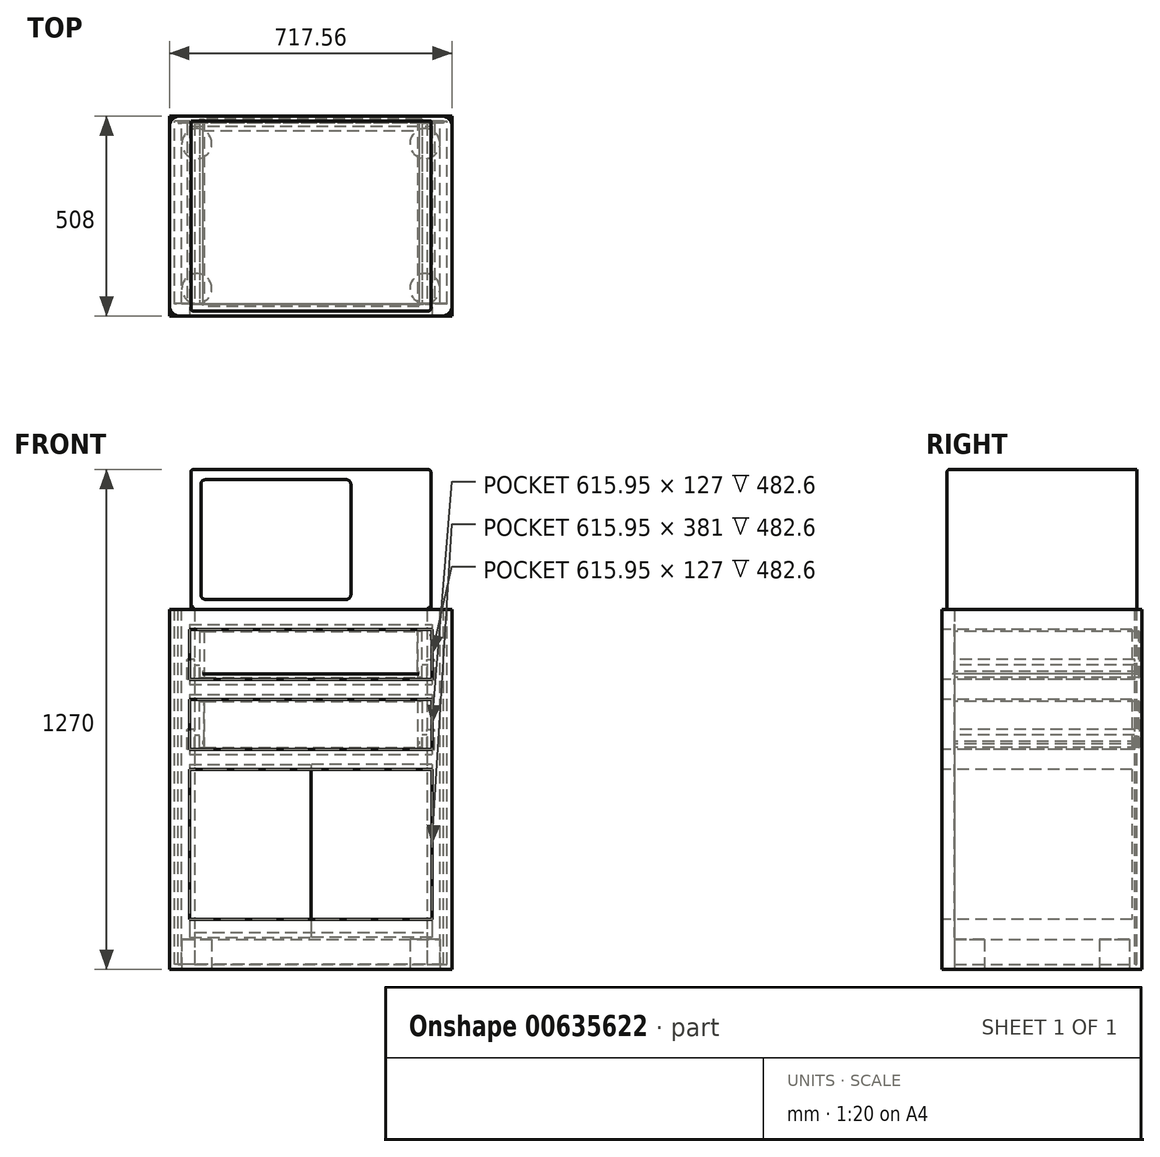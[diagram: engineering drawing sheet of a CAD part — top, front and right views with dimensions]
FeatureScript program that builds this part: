
annotation { "Feature Type Name" : "Feature", "Feature Type Description" : "" }
export const myFeature = defineFeature(function(context is Context, id is Id, definition is map)
    precondition{}
    {
        {
            assignVariable(context, id + "F0", {"name" : "ply_1_4", "anyValue" : 7 / 32});
        }
        {
            assignVariable(context, id + "F1", {"name" : "ply_1_2", "anyValue" : 15 / 32});
        }
        {
            assignVariable(context, id + "F2", {"name" : "ply_3_4", "anyValue" : 23 / 32});
        }
        {
            assignVariable(context, id + "F3", {"name" : "wood", "anyValue" : 3 / 4});
        }
        {
            var Q0;
            Q0=qCreatedBy(makeId("Top.planeOp"),FACE);
            cPlane(context, id + "F4", {"entities" : qUnion([Q0]), "cplaneType" : CPlaneType.OFFSET, "offset" : 914.4 * mm, "width" : 152.4 * mm, "height" : 152.4 * mm});
        }
        {
            var Q0;
            Q0=qCreatedBy(makeId("Top.planeOp"),FACE);
            cPlane(context, id + "F5", {"entities" : qUnion([Q0]), "cplaneType" : CPlaneType.OFFSET, "offset" : 12.7 * mm, "width" : 152.4 * mm, "height" : 152.4 * mm});
        }
        {
            var Q0;
            Q0=qCreatedBy(id+"F4.planeOp",FACE);
            var sketch = newSketch(context, id + "F6", { "sketchPlane" : qUnion([Q0])});
            skLineSegment(sketch, "E0.bottom", {"start": v(304.8, -241.3) * mm, "end": v(-304.8, -241.3) * mm});
            skLineSegment(sketch, "E0.top", {"start": v(304.8, 241.3) * mm, "end": v(-304.8, 241.3) * mm});
            skLineSegment(sketch, "E0.left", {"start": v(304.8, -241.3) * mm, "end": v(304.8, 241.3) * mm});
            skLineSegment(sketch, "E0.right", {"start": v(-304.8, -241.3) * mm, "end": v(-304.8, 241.3) * mm});
            skPoint(sketch, "E0.middle", {"position": v(0, 0) * mm});
            skSolve(sketch);
        }
        {
            var Q0;
            Q0=qSketchRegion(id+"F6",true);
            extrude(context, id + "F7", {"entities" : qUnion([Q0]), "depth" : 355.6 * mm, "offsetDistance" : 25.4 * mm});
        }
        {
            var Q0;
            Q0=makeQuery(id+"F7.opExtrude","SWEPT_FACE",FACE,{"disambiguationData":[OSD([sQuery(id+"F6.wireOp",EDGE,"E0.bottom")])]});
            var sketch = newSketch(context, id + "F8", { "sketchPlane" : qUnion([Q0])});
            skLineSegment(sketch, "E1.bottom", {"start": v(88.9, 939.8) * mm, "end": v(-266.7, 939.8) * mm});
            skLineSegment(sketch, "E1.top", {"start": v(88.9, 1244.6) * mm, "end": v(-266.7, 1244.6) * mm});
            skLineSegment(sketch, "E1.left", {"start": v(101.6, 952.5) * mm, "end": v(101.6, 1231.9) * mm});
            skLineSegment(sketch, "E1.right", {"start": v(-279.4, 952.5) * mm, "end": v(-279.4, 1231.9) * mm});
            skPoint(sketch, "E1.middle", {"position": v(-88.9, 1092.2) * mm});
            skPoint(sketch, "E2.visualSharp", {"position": v(-279.4, 1244.6) * mm});
            skArc(sketch, "E2.filletArc", {"start": v(-266.7, 1244.6) * mm, "mid": v(-275.68, 1240.88) * mm, "end": v(-279.4, 1231.9) * mm});
            skPoint(sketch, "E3.visualSharp", {"position": v(-279.4, 939.8) * mm});
            skArc(sketch, "E3.filletArc", {"start": v(-279.4, 952.5) * mm, "mid": v(-275.68, 943.52) * mm, "end": v(-266.7, 939.8) * mm});
            skPoint(sketch, "E4.visualSharp", {"position": v(101.6, 939.8) * mm});
            skArc(sketch, "E4.filletArc", {"start": v(88.9, 939.8) * mm, "mid": v(97.88, 943.52) * mm, "end": v(101.6, 952.5) * mm});
            skPoint(sketch, "E5.visualSharp", {"position": v(101.6, 1244.6) * mm});
            skArc(sketch, "E5.filletArc", {"start": v(101.6, 1231.9) * mm, "mid": v(97.88, 1240.88) * mm, "end": v(88.9, 1244.6) * mm});
            skSolve(sketch);
        }
        {
            var Q0;
            Q0 = qSketchRegion(id + "F8", true);
            extrude(context, id + "F9", {"entities" : qUnion([Q0]), "operationType" : NewBodyOperationType.REMOVE, "oppositeDirection" : true, "depth" : 1.59 * mm, "offsetDistance" : 25.4 * mm});
        }
        {
            var Q0;
            Q0=makeQuery(id+"F7.opExtrude","CAP_EDGE",EDGE,{"disambiguationData":[OSD([sQuery(id+"F6.wireOp",EDGE,"E0.right")])],"isStart":false});
            var Q1;
            Q1=makeQuery(id+"F7.opExtrude","CAP_EDGE",EDGE,{"disambiguationData":[OSD([sQuery(id+"F6.wireOp",EDGE,"E0.left")])],"isStart":false});
            var Q2;
            Q2=makeQuery(id+"F7.opExtrude","SWEPT_FACE",FACE,{"disambiguationData":[OSD([sQuery(id+"F6.wireOp",EDGE,"E0.bottom")])]});
            fillet(context, id + "F10", {"entities" : qUnion([Q0, Q1, Q2]), "radius" : 6.35 * mm, "tangentPropagation" : true, "allowEdgeOverflow" : false});
        }
        {
            var Q0;
            Q0=qCreatedBy(makeId("Top.planeOp"),FACE);
            var sketch = newSketch(context, id + "F11", { "sketchPlane" : qUnion([Q0])});
            skLineSegment(sketch, "E6.bottom", {"start": v(-358.78, -254) * mm, "end": v(358.78, -254) * mm});
            skLineSegment(sketch, "E6.top", {"start": v(-358.78, 254) * mm, "end": v(358.78, 254) * mm});
            skLineSegment(sketch, "E6.left", {"start": v(-358.78, -254) * mm, "end": v(-358.78, 254) * mm});
            skLineSegment(sketch, "E6.right", {"start": v(358.78, -254) * mm, "end": v(358.78, 254) * mm});
            skPoint(sketch, "E6.middle", {"position": v(0, 0) * mm});
            skSolve(sketch);
        }
        {
            var Q0;
            Q0=qSketchRegion(id+"F11",true);
            extrude(context, id + "F12", {"entities" : qUnion([Q0]), "depth" : 914.4 * mm, "offsetDistance" : 25.4 * mm});
        }
        {
            var Q0;
            Q0=makeQuery(id+"F12.opExtrude","SWEPT_FACE",FACE,{"disambiguationData":[OSD([sQuery(id+"F11.wireOp",EDGE,"E6.bottom")])]});
            var sketch = newSketch(context, id + "F13", { "sketchPlane" : qUnion([Q0])});
            skLineSegment(sketch, "E7.bottom", {"start": v(-307.98, 863.6) * mm, "end": v(307.98, 863.6) * mm});
            skLineSegment(sketch, "E7.top", {"start": v(-307.98, 736.6) * mm, "end": v(307.98, 736.6) * mm});
            skLineSegment(sketch, "E7.left", {"start": v(-307.98, 863.6) * mm, "end": v(-307.98, 736.6) * mm});
            skLineSegment(sketch, "E7.right", {"start": v(307.98, 863.6) * mm, "end": v(307.98, 736.6) * mm});
            skLineSegment(sketch, "E8.bottom", {"start": v(-307.98, 508) * mm, "end": v(307.98, 508) * mm});
            skLineSegment(sketch, "E8.top", {"start": v(-307.98, 127) * mm, "end": v(307.98, 127) * mm});
            skLineSegment(sketch, "E8.left", {"start": v(-307.98, 508) * mm, "end": v(-307.98, 127) * mm});
            skLineSegment(sketch, "E8.right", {"start": v(307.98, 508) * mm, "end": v(307.98, 127) * mm});
            skLineSegment(sketch, "E9.bottom", {"start": v(-307.98, 685.8) * mm, "end": v(307.98, 685.8) * mm});
            skLineSegment(sketch, "E9.top", {"start": v(-307.98, 558.8) * mm, "end": v(307.98, 558.8) * mm});
            skLineSegment(sketch, "E9.left", {"start": v(-307.98, 685.8) * mm, "end": v(-307.98, 558.8) * mm});
            skLineSegment(sketch, "E9.right", {"start": v(307.98, 685.8) * mm, "end": v(307.98, 558.8) * mm});
            skLineSegment(sketch, "E10.bottom", {"start": v(295.28, 850.9) * mm, "end": v(-295.28, 850.9) * mm, "construction": true});
            skLineSegment(sketch, "E10.top", {"start": v(295.28, 749.3) * mm, "end": v(-295.28, 749.3) * mm, "construction": true});
            skLineSegment(sketch, "E10.left", {"start": v(295.28, 850.9) * mm, "end": v(295.28, 749.3) * mm, "construction": true});
            skLineSegment(sketch, "E10.right", {"start": v(-295.28, 850.9) * mm, "end": v(-295.28, 749.3) * mm, "construction": true});
            skLineSegment(sketch, "E11.bottom", {"start": v(295.27, 673.1) * mm, "end": v(-295.28, 673.1) * mm, "construction": true});
            skLineSegment(sketch, "E11.top", {"start": v(295.27, 571.5) * mm, "end": v(-295.28, 571.5) * mm, "construction": true});
            skLineSegment(sketch, "E11.left", {"start": v(295.27, 673.1) * mm, "end": v(295.27, 571.5) * mm, "construction": true});
            skLineSegment(sketch, "E11.right", {"start": v(-295.28, 673.1) * mm, "end": v(-295.28, 571.5) * mm, "construction": true});
            skSolve(sketch);
        }
        {
            var Q0;
            Q0=qSketchRegion(id+"F13",true);
            extrude(context, id + "F14", {"entities" : qUnion([Q0]), "operationType" : NewBodyOperationType.REMOVE, "oppositeDirection" : true, "depth" : 482.6 * mm, "offsetDistance" : 25.4 * mm});
        }
        {
            var Q0;
            Q0=qCreatedBy(id+"F4.planeOp",FACE);
            var sketch = newSketch(context, id + "F15", { "sketchPlane" : qUnion([Q0])});
            skLineSegment(sketch, "E12.bottom", {"start": v(333.38, -254) * mm, "end": v(-333.38, -254) * mm});
            skLineSegment(sketch, "E12.top", {"start": v(333.38, 254) * mm, "end": v(-333.38, 254) * mm});
            skLineSegment(sketch, "E12.left", {"start": v(358.78, -228.6) * mm, "end": v(358.78, 228.6) * mm});
            skLineSegment(sketch, "E12.right", {"start": v(-358.78, -228.6) * mm, "end": v(-358.78, 228.6) * mm});
            skPoint(sketch, "E12.middle", {"position": v(0, 0) * mm});
            skPoint(sketch, "E13.visualSharp", {"position": v(-358.78, 254) * mm});
            skArc(sketch, "E13.filletArc", {"start": v(-333.38, 254) * mm, "mid": v(-351.34, 246.56) * mm, "end": v(-358.77, 228.6) * mm});
            skPoint(sketch, "E14.visualSharp", {"position": v(-358.77, -254) * mm});
            skArc(sketch, "E14.filletArc", {"start": v(-358.77, -228.6) * mm, "mid": v(-351.34, -246.56) * mm, "end": v(-333.38, -254) * mm});
            skPoint(sketch, "E15.visualSharp", {"position": v(358.78, -254) * mm});
            skArc(sketch, "E15.filletArc", {"start": v(333.38, -254) * mm, "mid": v(351.34, -246.56) * mm, "end": v(358.78, -228.6) * mm});
            skPoint(sketch, "E16.visualSharp", {"position": v(358.78, 254) * mm});
            skArc(sketch, "E16.filletArc", {"start": v(358.78, 228.6) * mm, "mid": v(351.34, 246.56) * mm, "end": v(333.38, 254) * mm});
            skSolve(sketch);
        }
        {
            var Q0;
            Q0 = qSketchRegion(id + "F15", true);
            extrude(context, id + "F16", {"entities" : qUnion([Q0]), "depth" : (getVariable(context, 'ply_3_4')) * mm, "offsetDistance" : 25.4 * mm});
        }
        {
            var Q0;
            Q0=qCreatedBy(id+"F4.planeOp",FACE);
            var sketch = newSketch(context, id + "F17", { "sketchPlane" : qUnion([Q0])});
            skLineSegment(sketch, "E17.left", {"start": v(-327.82, 235.74) * mm, "end": v(-327.82, -222.25) * mm});
            skLineSegment(sketch, "E17.right", {"start": v(-346.08, 241.3) * mm, "end": v(-346.08, -222.25) * mm});
            skPoint(sketch, "E17.middle", {"position": v(-336.95, 9.52) * mm});
            skLineSegment(sketch, "E18", {"start": v(-346.08, -222.25) * mm, "end": v(-327.82, -222.25) * mm});
            skLineSegment(sketch, "E19", {"start": v(-346.08, 241.3) * mm, "end": v(-337.34, 241.3) * mm});
            skLineSegment(sketch, "E20", {"start": v(-327.82, 235.74) * mm, "end": v(-337.34, 235.74) * mm});
            skLineSegment(sketch, "E21", {"start": v(-337.34, 235.74) * mm, "end": v(-337.34, 241.3) * mm});
            skLineSegment(sketch, "E22.bottom", {"start": v(-337.34, 235.74) * mm, "end": v(337.34, 235.74) * mm});
            skLineSegment(sketch, "E22.top", {"start": v(-337.34, 241.3) * mm, "end": v(337.34, 241.3) * mm});
            skLineSegment(sketch, "E22.right", {"start": v(337.34, 235.74) * mm, "end": v(337.34, 241.3) * mm});
            skLineSegment(sketch, "E23.MirrorCS", {"start": v(346.08, 241.3) * mm, "end": v(337.34, 241.3) * mm});
            skLineSegment(sketch, "E24.MirrorCS", {"start": v(327.82, 235.74) * mm, "end": v(337.34, 235.74) * mm});
            skLineSegment(sketch, "E25.MirrorCS", {"start": v(327.82, 235.74) * mm, "end": v(327.82, -222.25) * mm});
            skLineSegment(sketch, "E26.MirrorCS", {"start": v(346.08, 241.3) * mm, "end": v(346.08, -222.25) * mm});
            skPoint(sketch, "E27.MirrorP", {"position": v(336.95, 9.52) * mm});
            skLineSegment(sketch, "E28.MirrorCS", {"start": v(346.08, -222.25) * mm, "end": v(327.82, -222.25) * mm});
            skSolve(sketch);
        }
        {
            var Q0;
            Q0 = qSketchRegion(id + "F17", true);
            var Q1;
            Q1=qCreatedBy(id+"F5.planeOp",FACE);
            extrude(context, id + "F18", {"entities" : qUnion([Q0]), "endBound" : BoundingType.UP_TO_SURFACE, "oppositeDirection" : true, "depth" : 25.4 * mm, "endBoundEntityFace" : qUnion([Q1]), "offsetDistance" : 25.4 * mm});
        }
        {
            var Q0;
            Q0=qCreatedBy(makeId("Top.planeOp"),FACE);
            var sketch = newSketch(context, id + "F19", { "sketchPlane" : qUnion([Q0])});
            skCircle(sketch, "E29", {"center": v(-289.72, -184.15) * mm, "radius": 38.1 * mm});
            skCircle(sketch, "E30.MirrorC", {"center": v(289.72, -184.15) * mm, "radius": 38.1 * mm});
            skCircle(sketch, "E31.MirrorC", {"center": v(-289.72, 184.15) * mm, "radius": 38.1 * mm});
            skCircle(sketch, "E32.MirrorC", {"center": v(289.72, 184.15) * mm, "radius": 38.1 * mm});
            skSolve(sketch);
        }
        {
            var Q0;
            Q0 = qSketchRegion(id + "F19", true);
            extrude(context, id + "F20", {"entities" : qUnion([Q0]), "depth" : 76.2 * mm, "offsetDistance" : 25.4 * mm});
        }
        {
            var Q0;
            Q0=makeQuery(id+"F18.opExtrude","SWEPT_FACE",FACE,{"disambiguationData":[OSD([sQuery(id+"F17.wireOp",EDGE,"E18")])]});
            var sketch = newSketch(context, id + "F21", { "sketchPlane" : qUnion([Q0])});
            skLineSegment(sketch, "E33.0", {"start": v(-346.08, 12.7) * mm, "end": v(-346.08, 914.4) * mm});
            skLineSegment(sketch, "E34", {"start": v(-346.08, 914.4) * mm, "end": v(-295.28, 914.4) * mm});
            skLineSegment(sketch, "E35", {"start": v(-295.28, 914.4) * mm, "end": v(-295.28, 12.7) * mm});
            skLineSegment(sketch, "E36", {"start": v(-295.28, 12.7) * mm, "end": v(-346.08, 12.7) * mm});
            skLineSegment(sketch, "E37.MirrorCS", {"start": v(295.28, 12.7) * mm, "end": v(346.08, 12.7) * mm});
            skLineSegment(sketch, "E38.MirrorCS", {"start": v(346.08, 914.4) * mm, "end": v(295.28, 914.4) * mm});
            skLineSegment(sketch, "E39.MirrorCS", {"start": v(295.28, 914.4) * mm, "end": v(295.28, 12.7) * mm});
            skLineSegment(sketch, "E40.MirrorCS", {"start": v(346.08, 12.7) * mm, "end": v(346.08, 914.4) * mm});
            skLineSegment(sketch, "E41.bottom", {"start": v(-295.27, 914.4) * mm, "end": v(295.27, 914.4) * mm});
            skLineSegment(sketch, "E41.top", {"start": v(-295.27, 863.6) * mm, "end": v(295.27, 863.6) * mm});
            skLineSegment(sketch, "E41.left", {"start": v(-295.27, 914.4) * mm, "end": v(-295.27, 863.6) * mm});
            skLineSegment(sketch, "E41.right", {"start": v(295.27, 914.4) * mm, "end": v(295.27, 863.6) * mm});
            skLineSegment(sketch, "E42.bottom", {"start": v(-295.27, 736.6) * mm, "end": v(295.27, 736.6) * mm});
            skLineSegment(sketch, "E42.top", {"start": v(-295.27, 685.8) * mm, "end": v(295.27, 685.8) * mm});
            skLineSegment(sketch, "E42.left", {"start": v(-295.27, 736.6) * mm, "end": v(-295.27, 685.8) * mm});
            skLineSegment(sketch, "E42.right", {"start": v(295.27, 736.6) * mm, "end": v(295.27, 685.8) * mm});
            skLineSegment(sketch, "E43.bottom", {"start": v(-295.27, 558.8) * mm, "end": v(295.27, 558.8) * mm});
            skLineSegment(sketch, "E43.top", {"start": v(-295.27, 508) * mm, "end": v(295.27, 508) * mm});
            skLineSegment(sketch, "E43.left", {"start": v(-295.27, 558.8) * mm, "end": v(-295.27, 508) * mm});
            skLineSegment(sketch, "E43.right", {"start": v(295.27, 558.8) * mm, "end": v(295.27, 508) * mm});
            skLineSegment(sketch, "E44.bottom", {"start": v(-295.27, 94.46) * mm, "end": v(295.27, 94.46) * mm});
            skLineSegment(sketch, "E44.top", {"start": v(-295.27, 12.7) * mm, "end": v(295.27, 12.7) * mm});
            skLineSegment(sketch, "E44.left", {"start": v(-295.27, 94.46) * mm, "end": v(-295.27, 12.7) * mm});
            skLineSegment(sketch, "E44.right", {"start": v(295.27, 94.46) * mm, "end": v(295.27, 12.7) * mm});
            skSolve(sketch);
        }
        {
            var Q0;
            Q0 = qSketchRegion(id + "F21", true);
            extrude(context, id + "F22", {"entities" : qUnion([Q0]), "depth" : (getVariable(context, 'wood')) * mm, "offsetDistance" : 25.4 * mm});
        }
        {
            var Q0;
            Q0=makeQuery(id+"F20.opExtrude","CAP_FACE",FACE,{"disambiguationData":[OSD([sQuery(id+"F19.wireOp",EDGE,"E31.MirrorC")])],"isStart":false});
            var sketch = newSketch(context, id + "F23", { "sketchPlane" : qUnion([Q0])});
            skLineSegment(sketch, "E45.0", {"start": v(-327.82, -222.25) * mm, "end": v(-327.82, 235.74) * mm});
            skLineSegment(sketch, "E46.0", {"start": v(327.82, -222.25) * mm, "end": v(327.82, 235.74) * mm});
            skLineSegment(sketch, "E47", {"start": v(-327.82, -222.25) * mm, "end": v(327.82, -222.25) * mm});
            skLineSegment(sketch, "E48", {"start": v(327.82, 235.74) * mm, "end": v(-327.82, 235.74) * mm});
            skSolve(sketch);
        }
        {
            var Q0;
            Q0 = qSketchRegion(id + "F23", true);
            extrude(context, id + "F24", {"entities" : qUnion([Q0]), "depth" : (getVariable(context, 'ply_3_4')) * mm, "offsetDistance" : 25.4 * mm});
        }
        {
            var Q0;
            Q0=makeQuery(id+"F22.opExtrude","CAP_FACE",FACE,{"disambiguationData":[OSD([sQuery(id+"F21.wireOp",EDGE,"E33.0"),sQuery(id+"F21.wireOp",EDGE,"E34"),sQuery(id+"F21.wireOp",EDGE,"E35"),sQuery(id+"F21.wireOp",EDGE,"E36")])],"isStart":false});
            var sketch = newSketch(context, id + "F25", { "sketchPlane" : qUnion([Q0])});
            skLineSegment(sketch, "E49.bottom", {"start": v(-307.98, 876.3) * mm, "end": v(307.98, 876.3) * mm});
            skLineSegment(sketch, "E49.top", {"start": v(-307.98, 723.9) * mm, "end": v(307.98, 723.9) * mm});
            skLineSegment(sketch, "E49.left", {"start": v(-307.98, 876.3) * mm, "end": v(-307.98, 723.9) * mm});
            skLineSegment(sketch, "E49.right", {"start": v(307.98, 876.3) * mm, "end": v(307.98, 723.9) * mm});
            skLineSegment(sketch, "E50.bottom", {"start": v(-307.98, 698.5) * mm, "end": v(307.98, 698.5) * mm});
            skLineSegment(sketch, "E50.top", {"start": v(-307.98, 546.1) * mm, "end": v(307.98, 546.1) * mm});
            skLineSegment(sketch, "E50.left", {"start": v(-307.98, 698.5) * mm, "end": v(-307.98, 546.1) * mm});
            skLineSegment(sketch, "E50.right", {"start": v(307.98, 698.5) * mm, "end": v(307.98, 546.1) * mm});
            skLineSegment(sketch, "E51.bottom", {"start": v(-307.98, 520.7) * mm, "end": v(0, 520.7) * mm});
            skLineSegment(sketch, "E51.top", {"start": v(-307.98, 81.76) * mm, "end": v(0, 81.76) * mm});
            skLineSegment(sketch, "E51.left", {"start": v(-307.98, 520.7) * mm, "end": v(-307.98, 81.76) * mm});
            skLineSegment(sketch, "E51.right", {"start": v(0, 520.7) * mm, "end": v(0, 81.76) * mm});
            skLineSegment(sketch, "E52.MirrorCS", {"start": v(307.98, 81.76) * mm, "end": v(0, 81.76) * mm});
            skLineSegment(sketch, "E53.MirrorCS", {"start": v(307.98, 520.7) * mm, "end": v(0, 520.7) * mm});
            skLineSegment(sketch, "E54.MirrorCS", {"start": v(307.98, 520.7) * mm, "end": v(307.98, 81.76) * mm});
            skSolve(sketch);
        }
        {
            var Q0;
            Q0 = qSketchRegion(id + "F25", true);
            extrude(context, id + "F26", {"entities" : qUnion([Q0]), "depth" : (getVariable(context, 'wood')) * mm, "offsetDistance" : 25.4 * mm});
        }
        {
            var Q0;
            Q0=makeQuery(id+"F22.opExtrude","CAP_FACE",FACE,{"disambiguationData":[OSD([sQuery(id+"F21.wireOp",EDGE,"E33.0"),sQuery(id+"F21.wireOp",EDGE,"E34"),sQuery(id+"F21.wireOp",EDGE,"E35"),sQuery(id+"F21.wireOp",EDGE,"E36")])],"isStart":true});
            var sketch = newSketch(context, id + "F27", { "sketchPlane" : qUnion([Q0])});
            skLineSegment(sketch, "E55.bottom", {"start": v(-314.33, 787.4) * mm, "end": v(-295.28, 787.4) * mm});
            skLineSegment(sketch, "E55.top", {"start": v(-314.33, 736.6) * mm, "end": v(-295.28, 736.6) * mm});
            skLineSegment(sketch, "E55.left", {"start": v(-314.33, 787.4) * mm, "end": v(-314.33, 736.6) * mm});
            skLineSegment(sketch, "E55.right", {"start": v(-295.28, 787.4) * mm, "end": v(-295.28, 736.6) * mm});
            skLineSegment(sketch, "E56.bottom", {"start": v(-314.33, 609.6) * mm, "end": v(-295.28, 609.6) * mm});
            skLineSegment(sketch, "E56.top", {"start": v(-314.33, 558.8) * mm, "end": v(-295.28, 558.8) * mm});
            skLineSegment(sketch, "E56.left", {"start": v(-314.33, 609.6) * mm, "end": v(-314.33, 558.8) * mm});
            skLineSegment(sketch, "E56.right", {"start": v(-295.28, 609.6) * mm, "end": v(-295.28, 558.8) * mm});
            skLineSegment(sketch, "E57.MirrorCS", {"start": v(314.33, 558.8) * mm, "end": v(295.28, 558.8) * mm});
            skLineSegment(sketch, "E58.MirrorCS", {"start": v(314.33, 609.6) * mm, "end": v(295.28, 609.6) * mm});
            skLineSegment(sketch, "E59.MirrorCS", {"start": v(314.33, 736.6) * mm, "end": v(295.28, 736.6) * mm});
            skLineSegment(sketch, "E60.MirrorCS", {"start": v(314.33, 787.4) * mm, "end": v(295.28, 787.4) * mm});
            skLineSegment(sketch, "E61.MirrorCS", {"start": v(295.28, 609.6) * mm, "end": v(295.28, 558.8) * mm});
            skLineSegment(sketch, "E62.MirrorCS", {"start": v(295.28, 787.4) * mm, "end": v(295.28, 736.6) * mm});
            skLineSegment(sketch, "E63.MirrorCS", {"start": v(314.33, 609.6) * mm, "end": v(314.33, 558.8) * mm});
            skLineSegment(sketch, "E64.MirrorCS", {"start": v(314.33, 787.4) * mm, "end": v(314.33, 736.6) * mm});
            skSolve(sketch);
        }
        {
            var Q0;
            Q0 = qSketchRegion(id + "F27", true);
            var Q1;
            Q1=makeQuery(id+"F18.opExtrude","SWEPT_FACE",FACE,{"disambiguationData":[OSD([sQuery(id+"F17.wireOp",EDGE,"E22.bottom")])]});
            extrude(context, id + "F28", {"entities" : qUnion([Q0]), "endBound" : BoundingType.UP_TO_SURFACE, "depth" : 25.4 * mm, "endBoundEntityFace" : qUnion([Q1]), "offsetDistance" : 25.4 * mm});
        }
        {
            var Q0;
            Q0=makeQuery(id+"F28.opExtrude","CAP_FACE",FACE,{"disambiguationData":[OSD([sQuery(id+"F27.wireOp",EDGE,"E59.MirrorCS"),sQuery(id+"F27.wireOp",EDGE,"E60.MirrorCS"),sQuery(id+"F27.wireOp",EDGE,"E62.MirrorCS"),sQuery(id+"F27.wireOp",EDGE,"E64.MirrorCS")])],"isStart":true});
            var sketch = newSketch(context, id + "F29", { "sketchPlane" : qUnion([Q0])});
            skLineSegment(sketch, "E65.bottom", {"start": v(-295.28, 736.6) * mm, "end": v(-282.58, 736.6) * mm});
            skLineSegment(sketch, "E65.top", {"start": v(-295.28, 773.68) * mm, "end": v(-282.58, 773.68) * mm});
            skLineSegment(sketch, "E65.left", {"start": v(-295.28, 736.6) * mm, "end": v(-295.28, 773.68) * mm});
            skLineSegment(sketch, "E65.right", {"start": v(-282.58, 736.6) * mm, "end": v(-282.58, 773.68) * mm});
            skLineSegment(sketch, "E66.bottom", {"start": v(-295.28, 558.8) * mm, "end": v(-282.58, 558.8) * mm});
            skLineSegment(sketch, "E66.top", {"start": v(-295.28, 595.88) * mm, "end": v(-282.58, 595.88) * mm});
            skLineSegment(sketch, "E66.left", {"start": v(-295.28, 558.8) * mm, "end": v(-295.28, 595.88) * mm});
            skLineSegment(sketch, "E66.right", {"start": v(-282.58, 558.8) * mm, "end": v(-282.58, 595.88) * mm});
            skLineSegment(sketch, "E67.MirrorCS", {"start": v(295.28, 773.68) * mm, "end": v(282.58, 773.68) * mm});
            skLineSegment(sketch, "E68.MirrorCS", {"start": v(295.28, 736.6) * mm, "end": v(282.58, 736.6) * mm});
            skLineSegment(sketch, "E69.MirrorCS", {"start": v(295.28, 558.8) * mm, "end": v(282.58, 558.8) * mm});
            skLineSegment(sketch, "E70.MirrorCS", {"start": v(295.28, 595.88) * mm, "end": v(282.58, 595.88) * mm});
            skLineSegment(sketch, "E71.MirrorCS", {"start": v(282.58, 736.6) * mm, "end": v(282.58, 773.68) * mm});
            skLineSegment(sketch, "E72.MirrorCS", {"start": v(295.28, 736.6) * mm, "end": v(295.28, 773.68) * mm});
            skLineSegment(sketch, "E73.MirrorCS", {"start": v(282.58, 558.8) * mm, "end": v(282.58, 595.88) * mm});
            skLineSegment(sketch, "E74.MirrorCS", {"start": v(295.28, 558.8) * mm, "end": v(295.28, 595.88) * mm});
            skSolve(sketch);
        }
        {
            var Q0;
            Q0 = qSketchRegion(id + "F29", true);
            extrude(context, id + "F30", {"entities" : qUnion([Q0]), "oppositeDirection" : true, "depth" : 457.2 * mm, "offsetDistance" : 25.4 * mm});
        }
        {
            var Q0;
            Q0=makeQuery(id+"F22.opExtrude","CAP_FACE",FACE,{"disambiguationData":[OSD([sQuery(id+"F21.wireOp",EDGE,"E33.0"),sQuery(id+"F21.wireOp",EDGE,"E34"),sQuery(id+"F21.wireOp",EDGE,"E35"),sQuery(id+"F21.wireOp",EDGE,"E36")])],"isStart":false});
            var sketch = newSketch(context, id + "F31", { "sketchPlane" : qUnion([Q0])});
            skLineSegment(sketch, "E75.bottom", {"start": v(-282.58, 858.84) * mm, "end": v(-270.67, 858.84) * mm});
            skLineSegment(sketch, "E75.top", {"start": v(-282.58, 741.36) * mm, "end": v(-270.67, 741.36) * mm});
            skLineSegment(sketch, "E75.left", {"start": v(-282.58, 858.84) * mm, "end": v(-282.58, 741.36) * mm});
            skLineSegment(sketch, "E75.right", {"start": v(-270.67, 858.84) * mm, "end": v(-270.67, 756.44) * mm});
            skLineSegment(sketch, "E76", {"start": v(-270.67, 756.44) * mm, "end": v(-275.43, 756.44) * mm});
            skLineSegment(sketch, "E77", {"start": v(-275.43, 756.44) * mm, "end": v(-275.43, 750.89) * mm});
            skLineSegment(sketch, "E78", {"start": v(-275.43, 750.89) * mm, "end": v(-270.67, 750.89) * mm});
            skLineSegment(sketch, "E79.bottom", {"start": v(-282.58, 681.04) * mm, "end": v(-270.67, 681.04) * mm});
            skLineSegment(sketch, "E79.top", {"start": v(-282.58, 563.56) * mm, "end": v(-270.67, 563.56) * mm});
            skLineSegment(sketch, "E79.left", {"start": v(-282.58, 563.56) * mm, "end": v(-282.58, 681.04) * mm});
            skLineSegment(sketch, "E79.right", {"start": v(-270.67, 578.64) * mm, "end": v(-270.67, 681.04) * mm});
            skLineSegment(sketch, "E80", {"start": v(-270.67, 578.64) * mm, "end": v(-275.43, 578.64) * mm});
            skLineSegment(sketch, "E81", {"start": v(-275.43, 578.64) * mm, "end": v(-275.43, 573.09) * mm});
            skLineSegment(sketch, "E82", {"start": v(-270.67, 573.09) * mm, "end": v(-275.43, 573.09) * mm});
            skLineSegment(sketch, "E83.trimOffspring", {"start": v(-270.67, 563.56) * mm, "end": v(-270.67, 573.09) * mm});
            skLineSegment(sketch, "E84.MirrorCS", {"start": v(270.67, 756.44) * mm, "end": v(275.43, 756.44) * mm});
            skLineSegment(sketch, "E85.MirrorCS", {"start": v(270.67, 573.09) * mm, "end": v(275.43, 573.09) * mm});
            skLineSegment(sketch, "E86.MirrorCS", {"start": v(275.43, 578.64) * mm, "end": v(275.43, 573.09) * mm});
            skLineSegment(sketch, "E87.MirrorCS", {"start": v(270.67, 573.09) * mm, "end": v(270.67, 563.56) * mm});
            skLineSegment(sketch, "E88.MirrorCS", {"start": v(270.67, 578.64) * mm, "end": v(275.43, 578.64) * mm});
            skLineSegment(sketch, "E89.MirrorCS", {"start": v(275.43, 750.89) * mm, "end": v(270.67, 750.89) * mm});
            skLineSegment(sketch, "E90.MirrorCS", {"start": v(270.67, 750.89) * mm, "end": v(270.67, 741.36) * mm});
            skLineSegment(sketch, "E91.MirrorCS", {"start": v(275.43, 750.89) * mm, "end": v(275.43, 756.44) * mm});
            skLineSegment(sketch, "E92.MirrorCS", {"start": v(282.58, 681.04) * mm, "end": v(270.67, 681.04) * mm});
            skLineSegment(sketch, "E93.MirrorCS", {"start": v(282.58, 563.56) * mm, "end": v(270.67, 563.56) * mm});
            skLineSegment(sketch, "E94.MirrorCS", {"start": v(282.58, 858.84) * mm, "end": v(270.67, 858.84) * mm});
            skLineSegment(sketch, "E95.MirrorCS", {"start": v(282.58, 741.36) * mm, "end": v(270.67, 741.36) * mm});
            skLineSegment(sketch, "E96.MirrorCS", {"start": v(282.58, 681.04) * mm, "end": v(282.58, 563.56) * mm});
            skLineSegment(sketch, "E97.MirrorCS", {"start": v(270.67, 681.04) * mm, "end": v(270.67, 578.64) * mm});
            skLineSegment(sketch, "E98.MirrorCS", {"start": v(270.67, 756.44) * mm, "end": v(270.67, 858.84) * mm});
            skLineSegment(sketch, "E99.MirrorCS", {"start": v(282.58, 741.36) * mm, "end": v(282.58, 858.84) * mm});
            skLineSegment(sketch, "E100", {"start": v(-270.67, 750.89) * mm, "end": v(-270.67, 741.36) * mm});
            skSolve(sketch);
        }
        {
            var Q0;
            Q0 = qSketchRegion(id + "F31", true);
            extrude(context, id + "F32", {"entities" : qUnion([Q0]), "oppositeDirection" : true, "depth" : 469.9 * mm, "offsetDistance" : 25.4 * mm});
        }
        {
            var Q0;
            Q0=makeQuery(id+"F32.opExtrude","CAP_FACE",FACE,{"disambiguationData":[OSD([sQuery(id+"F31.wireOp",EDGE,"E75.bottom"),sQuery(id+"F31.wireOp",EDGE,"E75.top"),sQuery(id+"F31.wireOp",EDGE,"E75.left"),sQuery(id+"F31.wireOp",EDGE,"E75.right"),sQuery(id+"F31.wireOp",EDGE,"E76"),sQuery(id+"F31.wireOp",EDGE,"E77"),sQuery(id+"F31.wireOp",EDGE,"E78"),sQuery(id+"F31.wireOp",EDGE,"c8352356-f6f4-44b0-b135-f56cd745330c.trimOffspring")])],"isStart":true});
            var sketch = newSketch(context, id + "F33", { "sketchPlane" : qUnion([Q0])});
            skLineSegment(sketch, "E101.bottom", {"start": v(-270.67, 858.84) * mm, "end": v(270.67, 858.84) * mm});
            skLineSegment(sketch, "E101.top", {"start": v(-270.67, 741.36) * mm, "end": v(270.67, 741.36) * mm});
            skLineSegment(sketch, "E101.left", {"start": v(-270.67, 858.84) * mm, "end": v(-270.67, 741.36) * mm});
            skLineSegment(sketch, "E101.right", {"start": v(270.67, 858.84) * mm, "end": v(270.67, 741.36) * mm});
            skLineSegment(sketch, "E102.bottom", {"start": v(-270.67, 681.04) * mm, "end": v(270.67, 681.04) * mm});
            skLineSegment(sketch, "E102.top", {"start": v(-270.67, 563.56) * mm, "end": v(270.67, 563.56) * mm});
            skLineSegment(sketch, "E102.left", {"start": v(-270.67, 681.04) * mm, "end": v(-270.67, 563.56) * mm});
            skLineSegment(sketch, "E102.right", {"start": v(270.67, 681.04) * mm, "end": v(270.67, 563.56) * mm});
            skSolve(sketch);
        }
        {
            var Q0;
            Q0 = qSketchRegion(id + "F33", true);
            extrude(context, id + "F34", {"entities" : qUnion([Q0]), "oppositeDirection" : true, "depth" : (getVariable(context, 'ply_1_2')) * mm, "offsetDistance" : 25.4 * mm});
        }
        {
            var Q0;
            Q0=makeQuery(id+"F32.opExtrude","CAP_FACE",FACE,{"disambiguationData":[OSD([sQuery(id+"F31.wireOp",EDGE,"E84.MirrorCS"),sQuery(id+"F31.wireOp",EDGE,"E89.MirrorCS"),sQuery(id+"F31.wireOp",EDGE,"E90.MirrorCS"),sQuery(id+"F31.wireOp",EDGE,"E91.MirrorCS"),sQuery(id+"F31.wireOp",EDGE,"E94.MirrorCS"),sQuery(id+"F31.wireOp",EDGE,"E95.MirrorCS"),sQuery(id+"F31.wireOp",EDGE,"E98.MirrorCS"),sQuery(id+"F31.wireOp",EDGE,"E99.MirrorCS")])],"isStart":false});
            var sketch = newSketch(context, id + "F35", { "sketchPlane" : qUnion([Q0])});
            skLineSegment(sketch, "E103.0.0", {"start": v(270.67, 741.36) * mm, "end": v(270.67, 858.84) * mm});
            skLineSegment(sketch, "E103.0.1", {"start": v(270.67, 858.84) * mm, "end": v(-270.67, 858.84) * mm});
            skLineSegment(sketch, "E103.0.2", {"start": v(-270.67, 858.84) * mm, "end": v(-270.67, 741.36) * mm});
            skLineSegment(sketch, "E103.0.3", {"start": v(-270.67, 741.36) * mm, "end": v(270.67, 741.36) * mm});
            skLineSegment(sketch, "E104.0.0", {"start": v(270.67, 563.56) * mm, "end": v(270.67, 681.04) * mm});
            skLineSegment(sketch, "E104.0.1", {"start": v(270.67, 681.04) * mm, "end": v(-270.67, 681.04) * mm});
            skLineSegment(sketch, "E104.0.2", {"start": v(-270.67, 681.04) * mm, "end": v(-270.67, 563.56) * mm});
            skLineSegment(sketch, "E104.0.3", {"start": v(-270.67, 563.56) * mm, "end": v(270.67, 563.56) * mm});
            skSolve(sketch);
        }
        {
            var Q0;
            Q0 = qSketchRegion(id + "F35", true);
            extrude(context, id + "F36", {"entities" : qUnion([Q0]), "oppositeDirection" : true, "depth" : (getVariable(context, 'ply_1_2')) * mm, "offsetDistance" : 25.4 * mm});
        }
        {
            var Q0;
            Q0=makeQuery(id+"F32.opExtrude","SWEPT_FACE",FACE,{"disambiguationData":[OSD([sQuery(id+"F31.wireOp",EDGE,"E78")])]});
            var sketch = newSketch(context, id + "F37", { "sketchPlane" : qUnion([Q0])});
            skLineSegment(sketch, "E105.0", {"start": v(-275.43, 216.7) * mm, "end": v(-275.43, -229.4) * mm});
            skLineSegment(sketch, "E106.0", {"start": v(275.43, 216.7) * mm, "end": v(275.43, -229.4) * mm});
            skLineSegment(sketch, "E107.0", {"start": v(-270.67, 216.7) * mm, "end": v(270.67, 216.7) * mm});
            skLineSegment(sketch, "E108.0", {"start": v(346.08, 241.3) * mm, "end": v(346.08, -222.25) * mm});
            skLineSegment(sketch, "E108.1", {"start": v(-270.67, -229.4) * mm, "end": v(270.67, -229.4) * mm});
            skLineSegment(sketch, "E109", {"start": v(-270.67, -229.4) * mm, "end": v(-275.43, -229.4) * mm});
            skPoint(sketch, "E110.orphan", {"position": v(-275.43, -241.3) * mm});
            skLineSegment(sketch, "E111", {"start": v(270.67, -229.4) * mm, "end": v(275.43, -229.4) * mm});
            skPoint(sketch, "E112.orphan", {"position": v(275.43, -241.3) * mm});
            skLineSegment(sketch, "E113", {"start": v(270.67, 216.7) * mm, "end": v(275.43, 216.7) * mm});
            skPoint(sketch, "E114.orphan", {"position": v(275.43, 228.6) * mm});
            skLineSegment(sketch, "E115", {"start": v(-270.67, 216.7) * mm, "end": v(-275.43, 216.7) * mm});
            skPoint(sketch, "E116.orphan", {"position": v(-275.43, 228.6) * mm});
            skSolve(sketch);
        }
        {
            var Q0;
            Q0 = qSketchRegion(id + "F37", true);
            extrude(context, id + "F38", {"entities" : qUnion([Q0]), "depth" : (getVariable(context, 'ply_1_4')) * mm, "offsetDistance" : 25.4 * mm});
        }
    });
